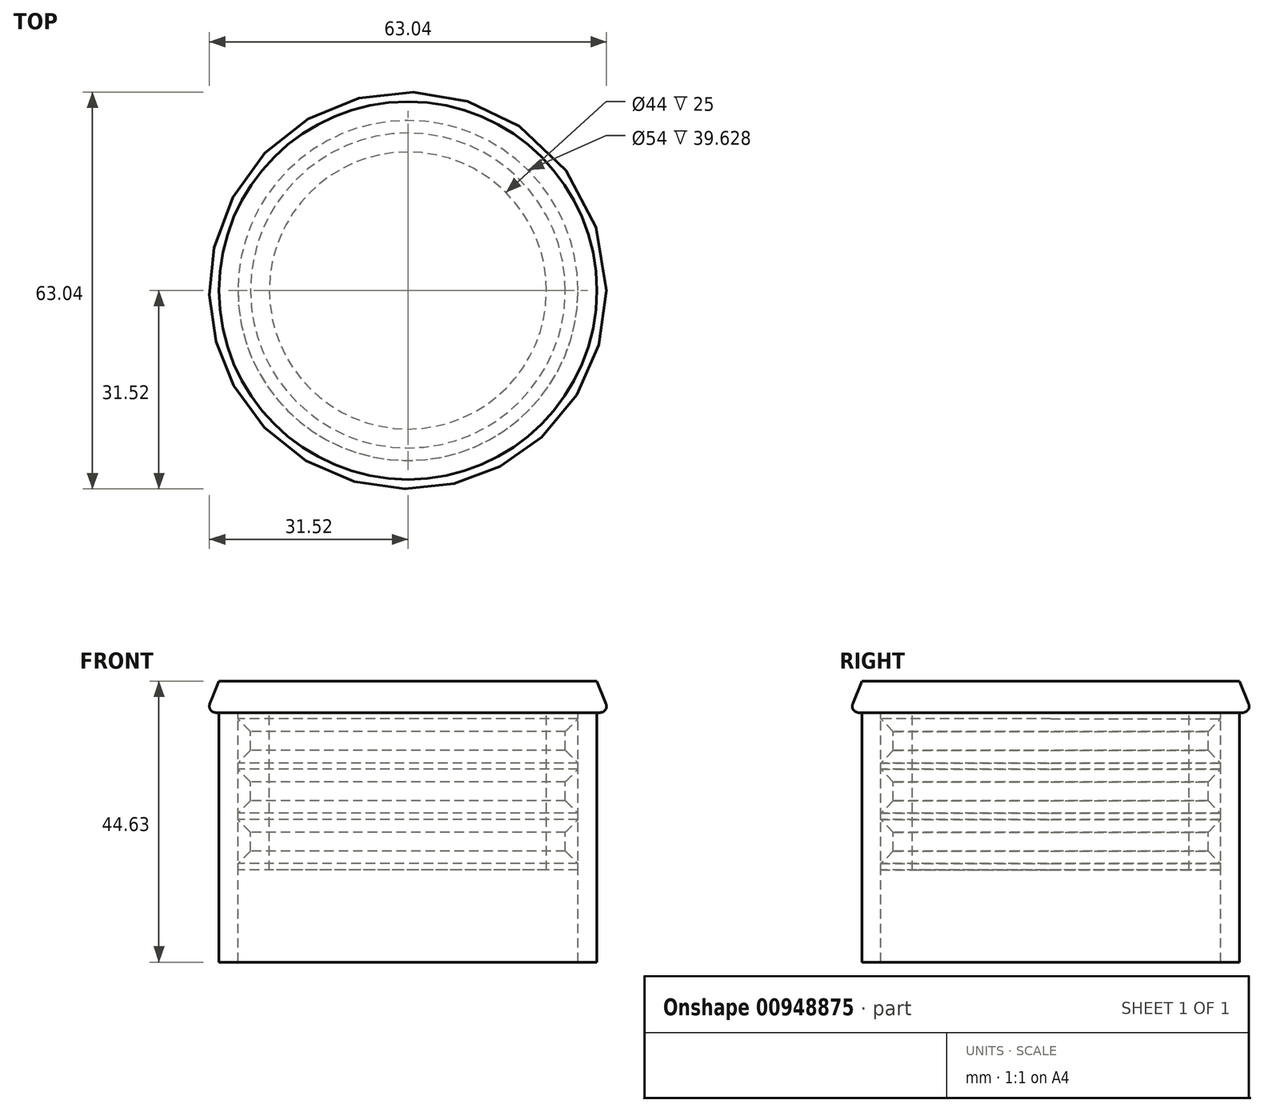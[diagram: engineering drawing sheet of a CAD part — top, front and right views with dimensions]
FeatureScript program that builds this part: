
annotation { "Feature Type Name" : "Feature", "Feature Type Description" : "" }
export const myFeature = defineFeature(function(context is Context, id is Id, definition is map)
    precondition{}
    {
        {
            var Q0;
            Q0=qCreatedBy(makeId("Front.planeOp"),FACE);
            var sketch = newSketch(context, id + "F0", { "sketchPlane" : qUnion([Q0])});
            skLineSegment(sketch, "E0.bottom", {"start": v(0, 0) * mm, "end": v(30, 0) * mm});
            skLineSegment(sketch, "E0.top", {"start": v(0, -39.63) * mm, "end": v(30, -39.63) * mm});
            skLineSegment(sketch, "E0.left", {"start": v(0, 0) * mm, "end": v(0, -39.63) * mm});
            skLineSegment(sketch, "E0.right", {"start": v(30, 0) * mm, "end": v(30, -39.63) * mm});
            skLineSegment(sketch, "E1.bottom", {"start": v(30, -39.63) * mm, "end": v(27, -39.63) * mm});
            skLineSegment(sketch, "E1.top", {"start": v(30, 0) * mm, "end": v(27, 0) * mm});
            skLineSegment(sketch, "E1.left", {"start": v(30, -39.63) * mm, "end": v(30, 0) * mm});
            skLineSegment(sketch, "E1.right", {"start": v(27, -39.63) * mm, "end": v(27, 0) * mm});
            skLineSegment(sketch, "E2.bottom", {"start": v(0, 0) * mm, "end": v(27, 0) * mm});
            skLineSegment(sketch, "E2.top", {"start": v(0, -25) * mm, "end": v(27, -25) * mm});
            skLineSegment(sketch, "E2.left", {"start": v(0, 0) * mm, "end": v(0, -25) * mm});
            skLineSegment(sketch, "E2.right", {"start": v(27, 0) * mm, "end": v(27, -25) * mm});
            skLineSegment(sketch, "E3.top", {"start": v(0, 5) * mm, "end": v(30, 5) * mm});
            skLineSegment(sketch, "E3.left", {"start": v(0, 0) * mm, "end": v(0, 5) * mm});
            skLineSegment(sketch, "E4.bottom", {"start": v(30, 5) * mm, "end": v(32, 5) * mm});
            skLineSegment(sketch, "E4.top", {"start": v(30, 0) * mm, "end": v(32, 0) * mm});
            skLineSegment(sketch, "E4.left", {"start": v(30, 5) * mm, "end": v(30, 0) * mm});
            skLineSegment(sketch, "E4.right", {"start": v(32, 5) * mm, "end": v(32, 0) * mm});
            skLineSegment(sketch, "E5.bottom", {"start": v(27, 0) * mm, "end": v(25, 0) * mm});
            skLineSegment(sketch, "E5.top", {"start": v(27, -3) * mm, "end": v(25, -3) * mm});
            skLineSegment(sketch, "E5.left", {"start": v(27, 0) * mm, "end": v(27, -3) * mm});
            skLineSegment(sketch, "E5.right", {"start": v(25, 0) * mm, "end": v(25, -3) * mm});
            skLineSegment(sketch, "E6.bottom", {"start": v(25, -3) * mm, "end": v(27, -3) * mm});
            skLineSegment(sketch, "E6.top", {"start": v(25, -6) * mm, "end": v(27, -6) * mm});
            skLineSegment(sketch, "E6.left", {"start": v(25, -3) * mm, "end": v(25, -6) * mm});
            skLineSegment(sketch, "E6.right", {"start": v(27, -3) * mm, "end": v(27, -6) * mm});
            skLineSegment(sketch, "E7.top", {"start": v(25, -11) * mm, "end": v(27, -11) * mm});
            skLineSegment(sketch, "E7.left", {"start": v(25, -6) * mm, "end": v(25, -11) * mm});
            skLineSegment(sketch, "E7.right", {"start": v(27, -6) * mm, "end": v(27, -11) * mm});
            skLineSegment(sketch, "E8.top", {"start": v(25, -14) * mm, "end": v(27, -14) * mm});
            skLineSegment(sketch, "E8.left", {"start": v(25, -11) * mm, "end": v(25, -14) * mm});
            skLineSegment(sketch, "E8.right", {"start": v(27, -11) * mm, "end": v(27, -14) * mm});
            skLineSegment(sketch, "E9.top", {"start": v(25, -19) * mm, "end": v(27, -19) * mm});
            skLineSegment(sketch, "E9.left", {"start": v(25, -14) * mm, "end": v(25, -19) * mm});
            skLineSegment(sketch, "E9.right", {"start": v(27, -14) * mm, "end": v(27, -19) * mm});
            skLineSegment(sketch, "E10.top", {"start": v(25, -22) * mm, "end": v(27, -22) * mm});
            skLineSegment(sketch, "E10.left", {"start": v(25, -19) * mm, "end": v(25, -22) * mm});
            skLineSegment(sketch, "E10.right", {"start": v(27, -19) * mm, "end": v(27, -22) * mm});
            skLineSegment(sketch, "E11.top", {"start": v(25, -25) * mm, "end": v(27, -25) * mm});
            skLineSegment(sketch, "E11.left", {"start": v(25, -22) * mm, "end": v(25, -25) * mm});
            skLineSegment(sketch, "E11.right", {"start": v(27, -22) * mm, "end": v(27, -25) * mm});
            skLineSegment(sketch, "E12.bottom", {"start": v(0, 0) * mm, "end": v(22, 0) * mm});
            skLineSegment(sketch, "E12.top", {"start": v(0, -25) * mm, "end": v(22, -25) * mm});
            skLineSegment(sketch, "E12.right", {"start": v(22, 0) * mm, "end": v(22, -25) * mm});
            skSolve(sketch);
        }
        {
            var Q0;
            {var subQ9=sQuery(id+"F0.wireOp",EDGE,"E0.right");Q0=makeQuery(id+"F0.imprint","IMPRINT",FACE,{"disambiguationData":[TD([[makeQuery(id+"F0.imprint","IMPRINT",EDGE,{"derivedFrom":subQ9}),-1.0]])]});}
            var Q1;
            Q1=sQuery(id+"F0.wireOp",EDGE,"E2.left");
            revolve(context, id + "F1", {"surfaceOperationType" : NewSurfaceOperationType.NEW, "entities" : qUnion([Q0]), "axis" : qUnion([Q1]), "revolveType" : RevolveType.FULL});
        }
        {
            var Q0;
            Q0=makeQuery(id+"F0.imprint","IMPRINT",FACE,{"disambiguationData":[TD([[makeQuery(id+"F0.imprint","IMPRINT",EDGE,{"derivedFrom":sQuery(id+"F0.wireOp",EDGE,"E3.top")}),-1.0]])]});
            var Q1;
            Q1=makeQuery(id+"F0.imprint","IMPRINT",FACE,{"disambiguationData":[TD([[makeQuery(id+"F0.imprint","IMPRINT",EDGE,{"derivedFrom":sQuery(id+"F0.wireOp",EDGE,"E4.bottom")}),-1.0]])]});
            var Q2;
            {var subQ3=sQuery(id+"F0.wireOp",EDGE,"E5.right");Q2=makeQuery(id+"F0.imprint","IMPRINT",FACE,{"disambiguationData":[TD([[makeQuery(id+"F0.imprint","IMPRINT",EDGE,{"derivedFrom":subQ3}),-1.0]])]});}
            var Q3;
            {var subQ4=sQuery(id+"F0.wireOp",EDGE,"E5.top");Q3=makeQuery(id+"F0.imprint","IMPRINT",FACE,{"disambiguationData":[TD([[makeQuery(id+"F0.imprint","IMPRINT",EDGE,{"derivedFrom":subQ4}),-1.0]])]});}
            var Q4;
            {var subQ0=sQuery(id+"F0.wireOp",EDGE,"E6.top");Q4=makeQuery(id+"F0.imprint","IMPRINT",FACE,{"disambiguationData":[TD([[makeQuery(id+"F0.imprint","IMPRINT",EDGE,{"derivedFrom":subQ0}),-1.0]])]});}
            var Q5;
            {var subQ0=sQuery(id+"F0.wireOp",EDGE,"E8.top");Q5=makeQuery(id+"F0.imprint","IMPRINT",FACE,{"disambiguationData":[TD([[makeQuery(id+"F0.imprint","IMPRINT",EDGE,{"derivedFrom":subQ0}),-1.0]])]});}
            var Q6;
            {var subQ0=sQuery(id+"F0.wireOp",EDGE,"E10.top");Q6=makeQuery(id+"F0.imprint","IMPRINT",FACE,{"disambiguationData":[TD([[makeQuery(id+"F0.imprint","IMPRINT",EDGE,{"derivedFrom":subQ0}),-1.0]])]});}
            var Q7;
            Q7=sQuery(id+"F0.wireOp",EDGE,"E2.left");
            revolve(context, id + "F2", {"surfaceOperationType" : NewSurfaceOperationType.NEW, "entities" : qUnion([Q0, Q1, Q2, Q3, Q4, Q5, Q6]), "axis" : qUnion([Q7]), "revolveType" : RevolveType.FULL});
        }
        {
            var Q0;
            Q0=makeQuery(id+"F2.opRevolve","SWEPT_EDGE",EDGE,{"disambiguationData":[OSD([sQuery(id+"F0.wireOp",EDGE,"E1.right"),sQuery(id+"F0.wireOp",EDGE,"E10.top")])]});
            var Q1;
            Q1=makeQuery(id+"F2.opRevolve","SWEPT_EDGE",EDGE,{"disambiguationData":[OSD([sQuery(id+"F0.wireOp",EDGE,"E1.right"),sQuery(id+"F0.wireOp",EDGE,"E9.top")])]});
            var Q2;
            Q2=makeQuery(id+"F2.opRevolve","SWEPT_EDGE",EDGE,{"disambiguationData":[OSD([sQuery(id+"F0.wireOp",EDGE,"E1.right"),sQuery(id+"F0.wireOp",EDGE,"E8.top")])]});
            var Q3;
            Q3=makeQuery(id+"F2.opRevolve","SWEPT_EDGE",EDGE,{"disambiguationData":[OSD([sQuery(id+"F0.wireOp",EDGE,"E1.right"),sQuery(id+"F0.wireOp",EDGE,"E6.top")])]});
            var Q4;
            Q4=makeQuery(id+"F2.opRevolve","SWEPT_EDGE",EDGE,{"disambiguationData":[OSD([sQuery(id+"F0.wireOp",EDGE,"E1.right"),sQuery(id+"F0.wireOp",EDGE,"E7.top")])]});
            var Q5;
            Q5=makeQuery(id+"F2.opRevolve","SWEPT_EDGE",EDGE,{"disambiguationData":[OSD([sQuery(id+"F0.wireOp",EDGE,"E1.right"),sQuery(id+"F0.wireOp",EDGE,"E5.top")])]});
            chamfer(context, id + "F3", {"entities" : qUnion([Q0, Q1, Q2, Q3, Q4, Q5]), "width" : 2 * mm, "tangentPropagation" : true});
        }
        {
            var Q0;
            Q0=makeQuery(id+"F2.opRevolve","SWEPT_EDGE",EDGE,{"disambiguationData":[OSD([sQuery(id+"F0.wireOp",EDGE,"E4.bottom"),sQuery(id+"F0.wireOp",EDGE,"E4.right")])]});
            chamfer(context, id + "F4", {"entities" : qUnion([Q0]), "chamferType" : ChamferType.TWO_OFFSETS, "width1" : 2 * mm, "oppositeDirection" : false, "width2" : 5 * mm, "tangentPropagation" : true});
        }
        {
            var Q0;
            Q0=makeQuery(id+"F4.opChamfer","BLEND_EDGE",EDGE,{"blendedFrom":[makeQuery(id+"F2.opRevolve","SWEPT_EDGE",EDGE,{"disambiguationData":[OSD([sQuery(id+"F0.wireOp",EDGE,"E4.bottom"),sQuery(id+"F0.wireOp",EDGE,"E4.right")])]}),makeQuery(id+"F2.opRevolve","SWEPT_FACE",FACE,{"disambiguationData":[OSD([sQuery(id+"F0.wireOp",EDGE,"E0.bottom"),sQuery(id+"F0.wireOp",EDGE,"E4.top")])]})],"blendedInto":[makeQuery(id+"F2.opRevolve","SWEPT_FACE",FACE,{"disambiguationData":[OSD([sQuery(id+"F0.wireOp",EDGE,"E0.bottom"),sQuery(id+"F0.wireOp",EDGE,"E4.top")])]})]});
            fillet(context, id + "F5", {"entities" : qUnion([Q0]), "radius" : 1 * mm, "tangentPropagation" : true, "allowEdgeOverflow" : false});
        }
    });
